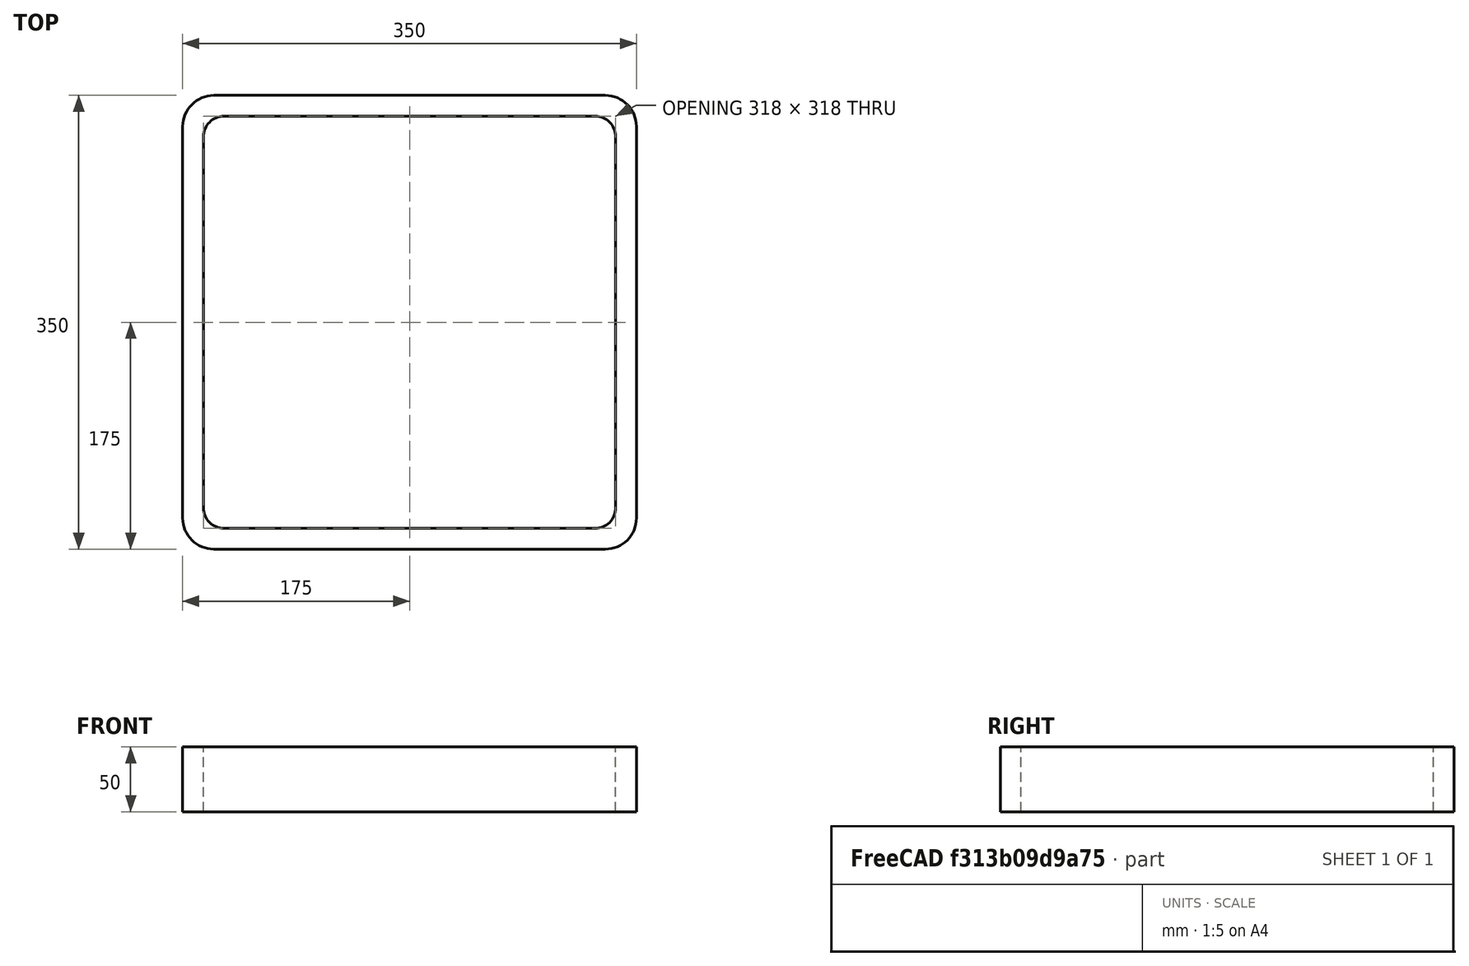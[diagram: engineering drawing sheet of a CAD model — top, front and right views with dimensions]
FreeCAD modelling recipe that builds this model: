
FCSTD DOCUMENT  (FreeCAD 0.15R4671 (Git))
Label: Square hollow section 350x350x16 EN10219 S235JRH
License: All rights reserved
LicenseURL: http://en.wikipedia.org/wiki/All_rights_reserved
objects: Sketcher::SketchObject×1, Part::Extrusion×1
note: 2 computed .brp shape members not serialized (recipe doc carries the construction recipe); baked Part::Feature solids carry a one-line shape summary decoded from their .brp

FEATURE [Sketcher::SketchObject] Sketch
  sketch-geometry (16):
    g0: LineSegment StartX=-143 StartY=159 StartZ=0 EndX=143 EndY=159 EndZ=0
    g1: LineSegment StartX=159 StartY=143 StartZ=0 EndX=159 EndY=-143 EndZ=0
    g2: LineSegment StartX=143 StartY=-159 StartZ=0 EndX=-143 EndY=-159 EndZ=0
    g3: LineSegment StartX=-159 StartY=-143 StartZ=0 EndX=-159 EndY=143 EndZ=0
    g4: LineSegment StartX=-151 StartY=175 StartZ=0 EndX=151 EndY=175 EndZ=0
    g5: LineSegment StartX=175 StartY=151 StartZ=0 EndX=175 EndY=-151 EndZ=0
    g6: LineSegment StartX=151 StartY=-175 StartZ=0 EndX=-151 EndY=-175 EndZ=0
    g7: LineSegment StartX=-175 StartY=-151 StartZ=0 EndX=-175 EndY=151 EndZ=0
    g8: ArcOfCircle CenterX=-143 CenterY=143 CenterZ=0 NormalX=0 NormalY=0 NormalZ=1 Radius=16 StartAngle=1.5708 EndAngle=3.14159
    g9: ArcOfCircle CenterX=143 CenterY=143 CenterZ=0 NormalX=0 NormalY=0 NormalZ=1 Radius=16 StartAngle=0 EndAngle=1.5708
    g10: ArcOfCircle CenterX=143 CenterY=-143 CenterZ=0 NormalX=0 NormalY=0 NormalZ=1 Radius=16 StartAngle=4.71239 EndAngle=6.28319
    g11: ArcOfCircle CenterX=-143 CenterY=-143 CenterZ=0 NormalX=0 NormalY=0 NormalZ=1 Radius=16 StartAngle=3.14159 EndAngle=4.71239
    g12: ArcOfCircle CenterX=151 CenterY=151 CenterZ=0 NormalX=0 NormalY=0 NormalZ=1 Radius=24 StartAngle=0 EndAngle=1.5708
    g13: ArcOfCircle CenterX=151 CenterY=-151 CenterZ=0 NormalX=0 NormalY=0 NormalZ=1 Radius=24 StartAngle=4.71239 EndAngle=6.28319
    g14: ArcOfCircle CenterX=-151 CenterY=-151 CenterZ=0 NormalX=0 NormalY=0 NormalZ=1 Radius=24 StartAngle=3.14159 EndAngle=4.71239
    g15: ArcOfCircle CenterX=-151 CenterY=151 CenterZ=0 NormalX=0 NormalY=0 NormalZ=1 Radius=24 StartAngle=1.5708 EndAngle=3.14159
  constraints (36):
    c: Horizontal(g2)
    c: Vertical(g3)
    c: Horizontal(g6)
    c: Vertical(g7)
    c: Tangent(g3,g8) = 1.5708
    c: Tangent(g0,g8) = 1.5708
    c: Tangent(g0,g9) = 1.5708
    c: Tangent(g1,g9) = 1.5708
    c: Tangent(g1,g10) = 1.5708
    c: Tangent(g2,g10) = 1.5708
    c: Tangent(g2,g11) = 1.5708
    c: Tangent(g3,g11) = 1.5708
    c: Tangent(g4,g12) = 1.5708
    c: Tangent(g5,g12) = 1.5708
    c: Tangent(g5,g13) = 1.5708
    c: Tangent(g6,g13) = 1.5708
    c: Tangent(g6,g14) = 1.5708
    c: Tangent(g7,g14) = 1.5708
    c: Tangent(g7,g15) = 1.5708
    c: Tangent(g4,g15) = 1.5708
    c: Equal(g9,g8)
    c: Equal(g9,g11)
    c: Equal(g9,g10)
    c: Equal(g12,g15)
    c: Equal(g12,g14)
    c: Equal(g12,g13)
    c: Symmetric(g4,g6,g-1)
    c: Symmetric(g7,g5,g-2)
    c: DistanceY(g4,g6) = -350
    c: DistanceX(g7,g5) = 350
    c: Symmetric(g3,g1,g-2)
    c: Symmetric(g0,g2,g-1)
    c: DistanceY(g0,g4) = 16
    c: DistanceX(g5,g1) = -16
    c: Radius(g9) = 16
    c: Radius(g12) = 24
FEATURE [Part::Extrusion] Extrude  label="Square hollow section 350x350x16 EN10219 S235JRH"
  Base = -> Sketch
  Dir = (0,0,50)
  Solid = true
